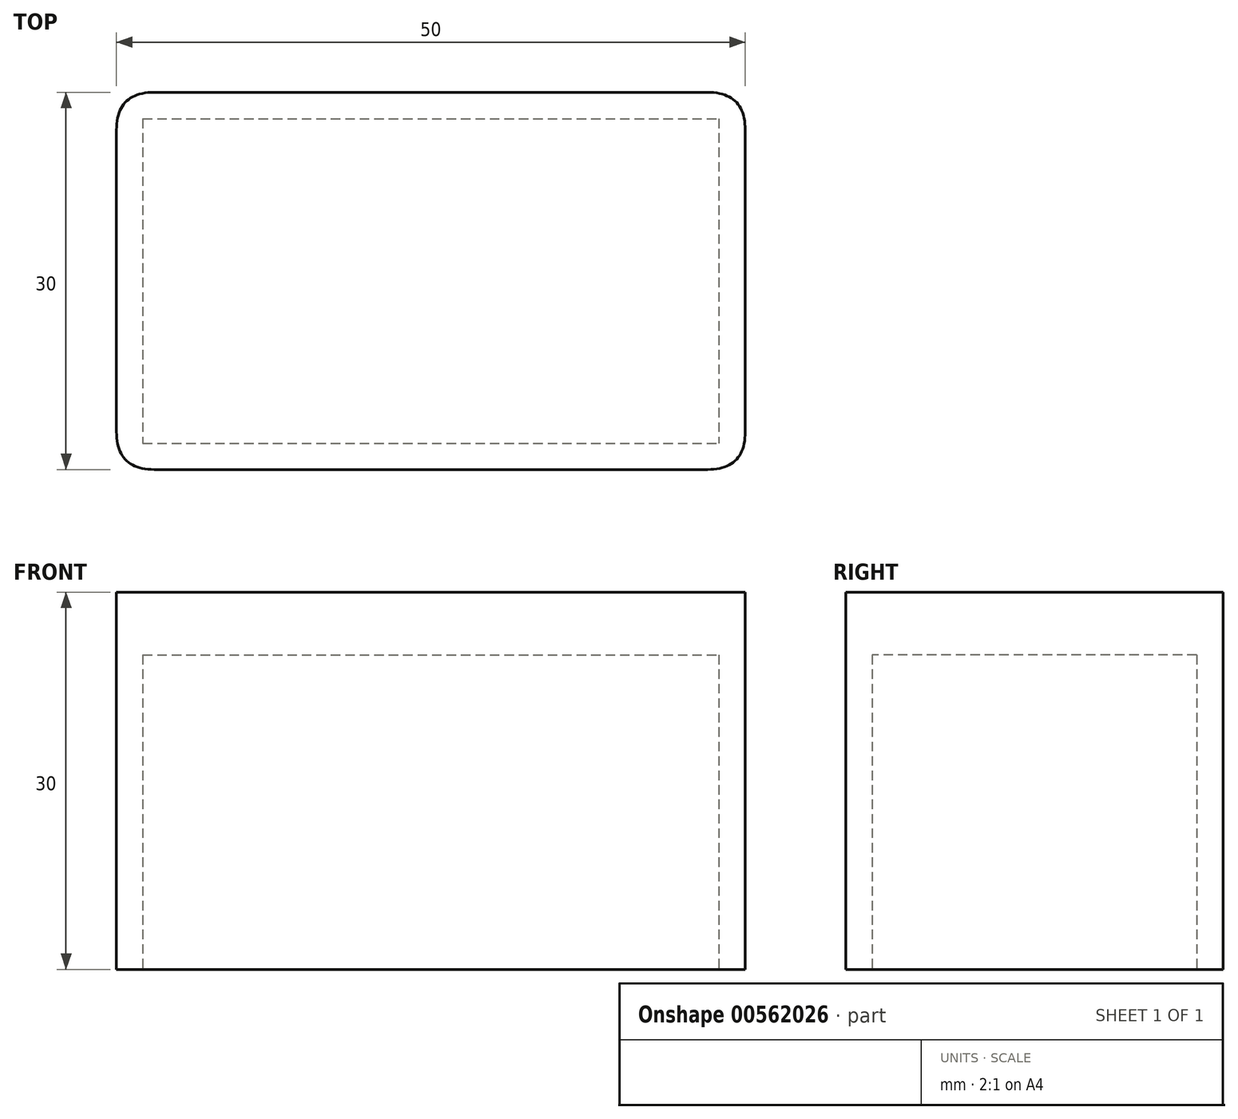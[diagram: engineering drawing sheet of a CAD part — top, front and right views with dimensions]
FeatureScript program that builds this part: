
annotation { "Feature Type Name" : "Feature", "Feature Type Description" : "" }
export const myFeature = defineFeature(function(context is Context, id is Id, definition is map)
    precondition{}
    {
        {
            var Q0;
            Q0=qCreatedBy(makeId("Top.planeOp"),FACE);
            var sketch = newSketch(context, id + "F0", { "sketchPlane" : qUnion([Q0])});
            skLineSegment(sketch, "E0.bottom", {"start": v(-20, 10) * mm, "end": v(20, 10) * mm});
            skLineSegment(sketch, "E0.top", {"start": v(-20, -10) * mm, "end": v(20, -10) * mm});
            skLineSegment(sketch, "E0.left", {"start": v(-20, 10) * mm, "end": v(-20, -10) * mm});
            skLineSegment(sketch, "E0.right", {"start": v(20, 10) * mm, "end": v(20, -10) * mm});
            skLineSegment(sketch, "E1.0", {"start": v(-25, 15) * mm, "end": v(25, 15) * mm});
            skLineSegment(sketch, "E1.1", {"start": v(-25, 15) * mm, "end": v(-25, -15) * mm});
            skLineSegment(sketch, "E1.2", {"start": v(-25, -15) * mm, "end": v(25, -15) * mm});
            skLineSegment(sketch, "E1.3", {"start": v(25, 15) * mm, "end": v(25, -15) * mm});
            skLineSegment(sketch, "E2.0", {"start": v(-22.5, 12.5) * mm, "end": v(-22.5, -12.5) * mm});
            skLineSegment(sketch, "E2.1", {"start": v(-22.5, 12.5) * mm, "end": v(22.5, 12.5) * mm});
            skLineSegment(sketch, "E2.2", {"start": v(22.5, 12.5) * mm, "end": v(22.5, -12.5) * mm});
            skLineSegment(sketch, "E2.3", {"start": v(-22.5, -12.5) * mm, "end": v(22.5, -12.5) * mm});
            skLineSegment(sketch, "E3.0", {"start": v(-22.9, 12.9) * mm, "end": v(-22.9, -12.9) * mm});
            skLineSegment(sketch, "E3.1", {"start": v(-22.9, 12.9) * mm, "end": v(22.9, 12.9) * mm});
            skLineSegment(sketch, "E3.2", {"start": v(22.9, 12.9) * mm, "end": v(22.9, -12.9) * mm});
            skLineSegment(sketch, "E3.3", {"start": v(-22.9, -12.9) * mm, "end": v(22.9, -12.9) * mm});
            skSolve(sketch);
        }
        {
            var Q0;
            Q0=makeQuery(id+"F0.imprint","IMPRINT",FACE,{"disambiguationData":[TD([[makeQuery(id+"F0.imprint","IMPRINT",EDGE,{"derivedFrom":sQuery(id+"F0.wireOp",EDGE,"E1.0")}),-1.0]])]});
            var Q1;
            Q1=makeQuery(id+"F0.imprint","IMPRINT",FACE,{"disambiguationData":[TD([[makeQuery(id+"F0.imprint","IMPRINT",EDGE,{"derivedFrom":sQuery(id+"F0.wireOp",EDGE,"E0.bottom")}),-1.0]])]});
            var Q2;
            Q2=makeQuery(id+"F0.imprint","IMPRINT",FACE,{"disambiguationData":[TD([[makeQuery(id+"F0.imprint","IMPRINT",EDGE,{"derivedFrom":sQuery(id+"F0.wireOp",EDGE,"E0.bottom")}),1.0]])]});
            var Q3;
            Q3=makeQuery(id+"F0.imprint","IMPRINT",FACE,{"disambiguationData":[TD([[makeQuery(id+"F0.imprint","IMPRINT",EDGE,{"derivedFrom":sQuery(id+"F0.wireOp",EDGE,"E2.0")}),-1.0]])]});
            extrude(context, id + "F1", {"entities" : qUnion([Q0, Q1, Q2, Q3]), "depth" : 30 * mm, "offsetDistance" : 25 * mm});
        }
        {
            var Q0;
            Q0=makeQuery(id+"F0.imprint","IMPRINT",FACE,{"disambiguationData":[TD([[makeQuery(id+"F0.imprint","IMPRINT",EDGE,{"derivedFrom":sQuery(id+"F0.wireOp",EDGE,"E0.bottom")}),-1.0]])]});
            var Q1;
            Q1=makeQuery(id+"F0.imprint","IMPRINT",FACE,{"disambiguationData":[TD([[makeQuery(id+"F0.imprint","IMPRINT",EDGE,{"derivedFrom":sQuery(id+"F0.wireOp",EDGE,"E0.bottom")}),1.0]])]});
            var Q2;
            Q2=makeQuery(id+"F0.imprint","IMPRINT",FACE,{"disambiguationData":[TD([[makeQuery(id+"F0.imprint","IMPRINT",EDGE,{"derivedFrom":sQuery(id+"F0.wireOp",EDGE,"E2.0")}),-1.0]])]});
            extrude(context, id + "F2", {"entities" : qUnion([Q0, Q1, Q2]), "operationType" : NewBodyOperationType.REMOVE, "depth" : 25 * mm, "offsetDistance" : 25 * mm});
        }
        {
            var Q0;
            Q0=makeQuery(id+"F1.opExtrude","SWEPT_EDGE",EDGE,{"disambiguationData":[OSD([sQuery(id+"F0.wireOp",EDGE,"E1.1"),sQuery(id+"F0.wireOp",EDGE,"E1.2")])]});
            var Q1;
            Q1=makeQuery(id+"F1.opExtrude","SWEPT_EDGE",EDGE,{"disambiguationData":[OSD([sQuery(id+"F0.wireOp",EDGE,"E1.0"),sQuery(id+"F0.wireOp",EDGE,"E1.1")])]});
            var Q2;
            Q2=makeQuery(id+"F1.opExtrude","SWEPT_EDGE",EDGE,{"disambiguationData":[OSD([sQuery(id+"F0.wireOp",EDGE,"E1.2"),sQuery(id+"F0.wireOp",EDGE,"E1.3")])]});
            var Q3;
            Q3=makeQuery(id+"F1.opExtrude","SWEPT_EDGE",EDGE,{"disambiguationData":[OSD([sQuery(id+"F0.wireOp",EDGE,"E1.0"),sQuery(id+"F0.wireOp",EDGE,"E1.3")])]});
            fillet(context, id + "F3", {"entities" : qUnion([Q0, Q1, Q2, Q3]), "radius" : 3 * mm, "tangentPropagation" : true, "rho" : 0.5, "crossSection" : FilletCrossSection.CONIC, "allowEdgeOverflow" : false});
        }
    });
